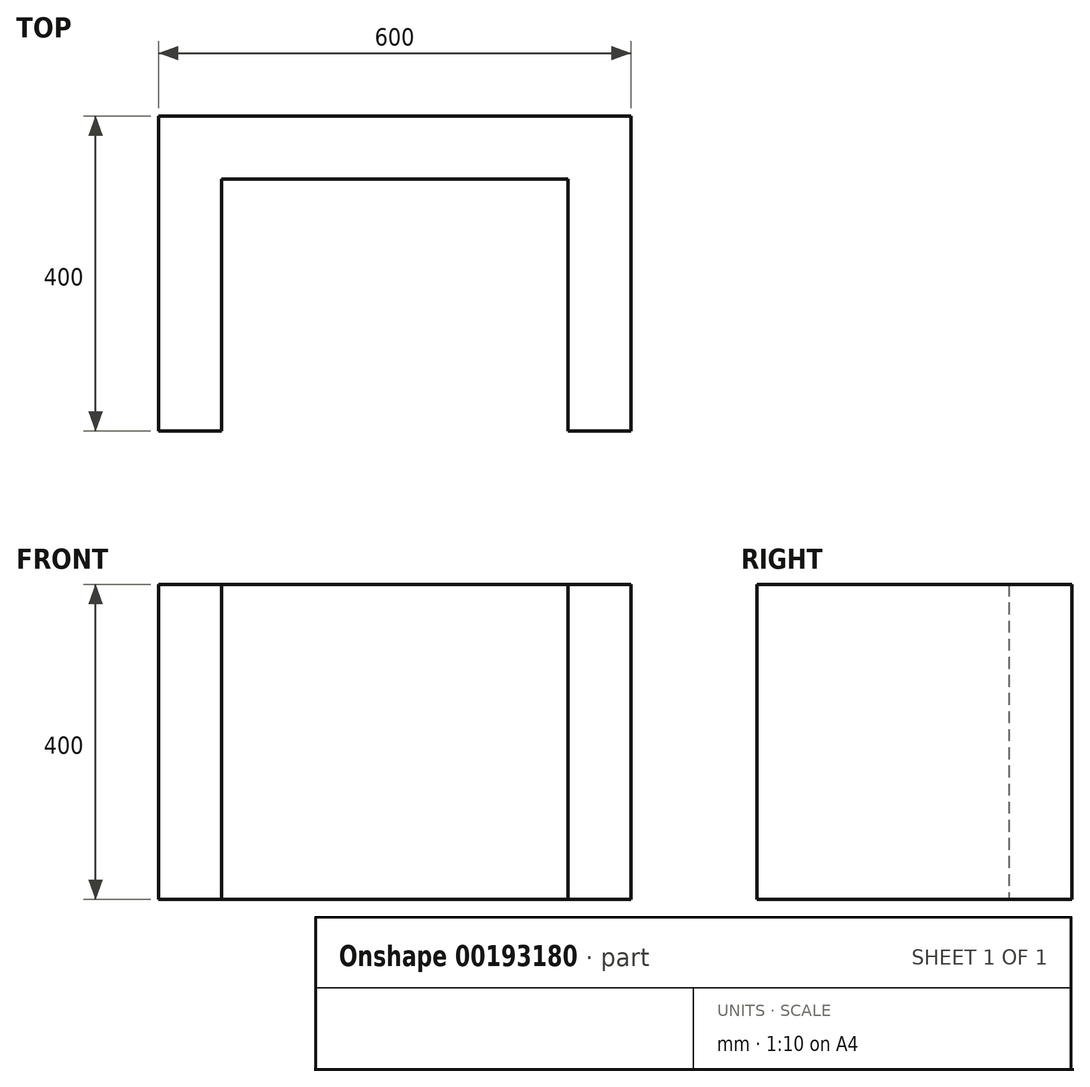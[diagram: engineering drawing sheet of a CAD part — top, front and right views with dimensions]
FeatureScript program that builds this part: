
annotation { "Feature Type Name" : "Feature", "Feature Type Description" : "" }
export const myFeature = defineFeature(function(context is Context, id is Id, definition is map)
    precondition{}
    {
        {
            var Q0;
            Q0=qCreatedBy(makeId("Top.planeOp"),FACE);
            var sketch = newSketch(context, id + "F0", { "sketchPlane" : qUnion([Q0])});
            skLineSegment(sketch, "E0", {"start": v(-300, 80) * mm, "end": v(-300, -320) * mm});
            skLineSegment(sketch, "E1", {"start": v(-300, -320) * mm, "end": v(-220, -320) * mm});
            skLineSegment(sketch, "E2", {"start": v(-220, -320) * mm, "end": v(-220, 0) * mm});
            skLineSegment(sketch, "E3", {"start": v(-220, 0) * mm, "end": v(220, 0) * mm});
            skLineSegment(sketch, "E4", {"start": v(220, 0) * mm, "end": v(220, -320) * mm});
            skLineSegment(sketch, "E5", {"start": v(220, -320) * mm, "end": v(300, -320) * mm});
            skLineSegment(sketch, "E6", {"start": v(300, -320) * mm, "end": v(300, 80) * mm});
            skLineSegment(sketch, "E7", {"start": v(300, 80) * mm, "end": v(-300, 80) * mm});
            skSolve(sketch);
        }
        {
            var Q0;
            Q0 = qSketchRegion(id + "F0", true);
            extrude(context, id + "F1", {"entities" : qUnion([Q0]), "depth" : 400 * mm});
        }
    });
